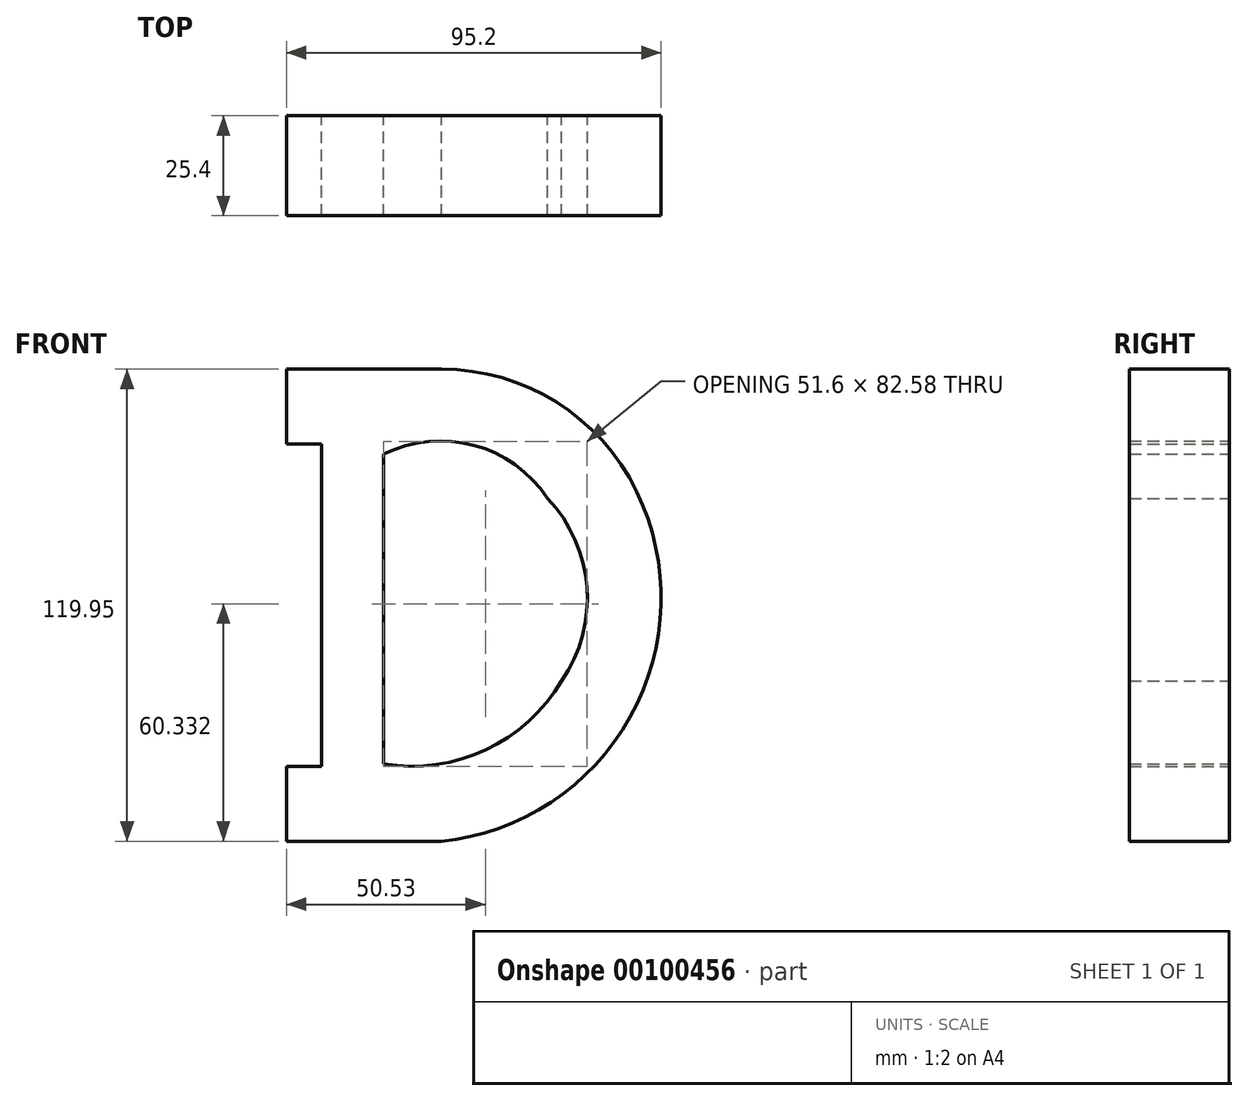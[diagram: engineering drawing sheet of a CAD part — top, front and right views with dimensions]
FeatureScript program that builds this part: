
annotation { "Feature Type Name" : "Feature", "Feature Type Description" : "" }
export const myFeature = defineFeature(function(context is Context, id is Id, definition is map)
    precondition{}
    {
        {
            var Q0;
            Q0=qCreatedBy(makeId("Front.planeOp"),FACE);
            var sketch = newSketch(context, id + "F0", { "sketchPlane" : qUnion([Q0])});
            skLineSegment(sketch, "E0", {"start": v(-54.58, 56.6) * mm, "end": v(-74.9, 56.6) * mm});
            skLineSegment(sketch, "E1", {"start": v(-74.9, 56.6) * mm, "end": v(-74.9, 37.55) * mm});
            skLineSegment(sketch, "E2", {"start": v(-74.9, 37.55) * mm, "end": v(-66, 37.55) * mm});
            skLineSegment(sketch, "E3", {"start": v(-66, 37.55) * mm, "end": v(-66, -44.3) * mm});
            skLineSegment(sketch, "E4", {"start": v(-66, -44.3) * mm, "end": v(-74.9, -44.3) * mm});
            skLineSegment(sketch, "E5", {"start": v(-74.9, -44.3) * mm, "end": v(-74.9, -63.35) * mm});
            skLineSegment(sketch, "E6", {"start": v(-74.9, -63.35) * mm, "end": v(-54.58, -63.35) * mm});
            skLineSegment(sketch, "E7", {"start": v(-54.58, 56.6) * mm, "end": v(-35.53, 56.6) * mm});
            skLineSegment(sketch, "E8", {"start": v(-54.58, -63.35) * mm, "end": v(-35.53, -63.35) * mm});
            skArc(sketch, "E9", {"start": v(-35.53, 56.6) * mm, "mid": v(-6.28, 48.2) * mm, "end": v(14.05, 25.57) * mm});
            skArc(sketch, "E10", {"start": v(14.05, 25.57) * mm, "mid": v(12.43, -31.81) * mm, "end": v(-35.53, -63.35) * mm});
            skSolve(sketch);
        }
        {
            var Q0;
            Q0=makeQuery(id+"F0.imprint","IMPRINT",FACE,{"disambiguationData":[TD([[makeQuery(id+"F0.imprint","IMPRINT",EDGE,{"derivedFrom":sQuery(id+"F0.wireOp",EDGE,"E0")}),1.0]])]});
            var sketch = newSketch(context, id + "F1", { "sketchPlane" : qUnion([Q0])});
            skLineSegment(sketch, "E11", {"start": v(-50.17, 35) * mm, "end": v(-50.17, -43.74) * mm});
            skArc(sketch, "E12", {"start": v(-8.56, 23.76) * mm, "mid": v(-27.24, 37.26) * mm, "end": v(-50.17, 35) * mm});
            skArc(sketch, "E13", {"start": v(-4.97, -22.6) * mm, "mid": v(1.43, 1.2) * mm, "end": v(-8.56, 23.76) * mm});
            skArc(sketch, "E14", {"start": v(-50.17, -43.74) * mm, "mid": v(-24.31, -40.14) * mm, "end": v(-4.97, -22.6) * mm});
            skSolve(sketch);
        }
        {
            var Q0;
            Q0=makeQuery(id+"F0.imprint","IMPRINT",FACE,{"disambiguationData":[TD([[makeQuery(id+"F0.imprint","IMPRINT",EDGE,{"derivedFrom":sQuery(id+"F0.wireOp",EDGE,"E0")}),1.0]])]});
            extrude(context, id + "F2", {"entities" : qUnion([Q0]), "depth" : 25.4 * mm});
        }
        {
            var Q0;
            Q0=makeQuery(id+"F1.imprint","IMPRINT",FACE,{"disambiguationData":[TD([[makeQuery(id+"F1.imprint","IMPRINT",EDGE,{"derivedFrom":sQuery(id+"F1.wireOp",EDGE,"E11")}),1.0]])]});
            extrude(context, id + "F3", {"entities" : qUnion([Q0]), "operationType" : NewBodyOperationType.REMOVE, "depth" : 25.4 * mm});
        }
    });
